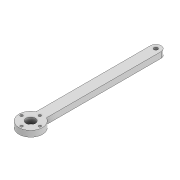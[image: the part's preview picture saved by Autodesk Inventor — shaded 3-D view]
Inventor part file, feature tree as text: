
AUTODESK INVENTOR PART (.ipt)
format: ipt  version: 2022 (Build 260153000, 153)  size: 113,152 bytes
history: native  units: mm
features: extrude x2, sketch x2, projected_geometry x1
ambient origin geometry x8: Origin, YZ Plane, XZ Plane, XY Plane, X Axis, Y Axis, Z Axis, Center Point
bodies: Solid1 (feature_tree)
feature tree (5):
  extrude  "Extrusion1"  Depth=7.1mm
  extrude  "Extrusion4"  Depth=7.0mm
  sketch  "Sketch1"  dims[d0=18.0mm d1=7.1mm]
  sketch  "Sketch4"  dims[d2=2.0mm d3=7.0mm d4=40.0mm d6=360.0deg d8=4.5mm d9=0.0mm d19=95.811mm d20=8.0mm d21=3.0mm d22=4.5mm d23=0.0mm]
  projected_geometry  "Projected Loop3"
